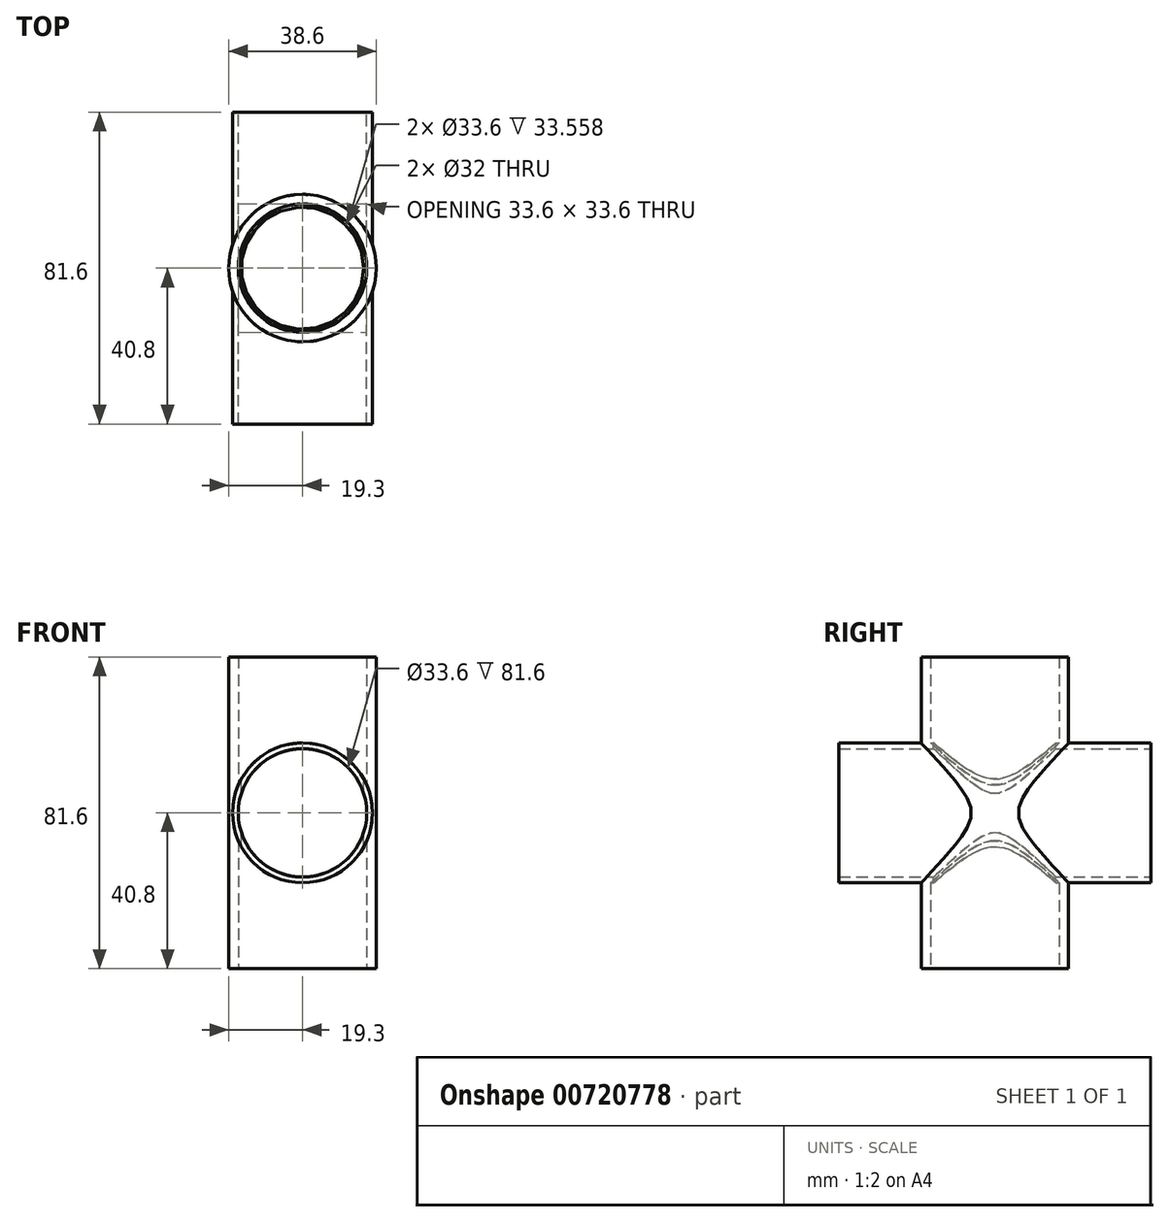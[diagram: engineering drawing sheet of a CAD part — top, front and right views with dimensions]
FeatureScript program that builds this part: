
annotation { "Feature Type Name" : "Feature", "Feature Type Description" : "" }
export const myFeature = defineFeature(function(context is Context, id is Id, definition is map)
    precondition{}
    {
        {
            var Q0;
            Q0=qCreatedBy(makeId("Top.planeOp"),FACE);
            var sketch = newSketch(context, id + "F0", { "sketchPlane" : qUnion([Q0])});
            skCircle(sketch, "E0", {"center": v(0, 0) * mm, "radius": 16.8 * mm});
            skCircle(sketch, "E1", {"center": v(0, 0) * mm, "radius": 19.3 * mm});
            skSolve(sketch);
        }
        {
            var Q0;
            Q0=makeQuery(id+"F0.imprint","IMPRINT",FACE,{"disambiguationData":[TD([[makeQuery(id+"F0.imprint","IMPRINT",EDGE,{"derivedFrom":sQuery(id+"F0.wireOp",EDGE,"E0")}),-1.0]])]});
            extrude(context, id + "F1", {"entities" : qUnion([Q0]), "depth" : 81.6 * mm, "offsetDistance" : 25 * mm});
        }
        {
            var Q0;
            Q0=qCreatedBy(makeId("Front.planeOp"),FACE);
            var sketch = newSketch(context, id + "F2", { "sketchPlane" : qUnion([Q0])});
            skLineSegment(sketch, "E2", {"start": v(0, 0) * mm, "end": v(0, 40.8) * mm, "construction": true});
            skCircle(sketch, "E3", {"center": v(0, 40.8) * mm, "radius": 16.8 * mm});
            skCircle(sketch, "E4", {"center": v(0, 40.8) * mm, "radius": 18.3 * mm});
            skSolve(sketch);
        }
        {
            var Q0;
            Q0=makeQuery(id+"F2.imprint","IMPRINT",FACE,{"disambiguationData":[TD([[makeQuery(id+"F2.imprint","IMPRINT",EDGE,{"derivedFrom":sQuery(id+"F2.wireOp",EDGE,"E3")}),-1.0]])]});
            extrude(context, id + "F3", {"entities" : qUnion([Q0]), "operationType" : NewBodyOperationType.ADD, "endBound" : BoundingType.SYMMETRIC, "depth" : 81.6 * mm, "offsetDistance" : 25 * mm});
        }
        {
            var Q0;
            Q0=makeQuery(id+"F1.opExtrude","CAP_FACE",FACE,{"disambiguationData":[OSD([sQuery(id+"F0.wireOp",EDGE,"E0"),sQuery(id+"F0.wireOp",EDGE,"E1")])],"isStart":false});
            var sketch = newSketch(context, id + "F4", { "sketchPlane" : qUnion([Q0])});
            skCircle(sketch, "E5", {"center": v(0, 0) * mm, "radius": 16 * mm});
            skSolve(sketch);
        }
        {
            var Q0;
            Q0=makeQuery(id+"F4.imprint","IMPRINT",FACE,{"disambiguationData":[TD([[makeQuery(id+"F4.imprint","IMPRINT",EDGE,{"derivedFrom":sQuery(id+"F4.wireOp",EDGE,"E5")}),1.0]])]});
            extrude(context, id + "F5", {"entities" : qUnion([Q0]), "operationType" : NewBodyOperationType.REMOVE, "oppositeDirection" : true, "depth" : 67.8 * mm, "offsetDistance" : 25 * mm});
        }
        {
            var Q0;
            Q0=makeQuery(id+"F3.opExtrude","CAP_FACE",FACE,{"disambiguationData":[OSD([sQuery(id+"F2.wireOp",EDGE,"E3"),sQuery(id+"F2.wireOp",EDGE,"E4")])],"isStart":false});
            var sketch = newSketch(context, id + "F6", { "sketchPlane" : qUnion([Q0])});
            skCircle(sketch, "E6", {"center": v(0, 40.8) * mm, "radius": 16 * mm});
            skSolve(sketch);
        }
        {
            var Q0;
            Q0=makeQuery(id+"F6.imprint","IMPRINT",FACE,{"disambiguationData":[TD([[makeQuery(id+"F6.imprint","IMPRINT",EDGE,{"derivedFrom":sQuery(id+"F6.wireOp",EDGE,"E6")}),1.0]])]});
            var Q1;
            Q1=makeQuery(id+"F6.imprint","IMPRINT",FACE,{"disambiguationData":[TD([[makeQuery(id+"F6.imprint","IMPRINT",EDGE,{"derivedFrom":sQuery(id+"F6.wireOp",EDGE,"E6")}),-1.0]])]});
            extrude(context, id + "F7", {"entities" : qUnion([Q0, Q1]), "operationType" : NewBodyOperationType.REMOVE, "oppositeDirection" : true, "depth" : 68 * mm, "offsetDistance" : 25 * mm});
        }
    });
